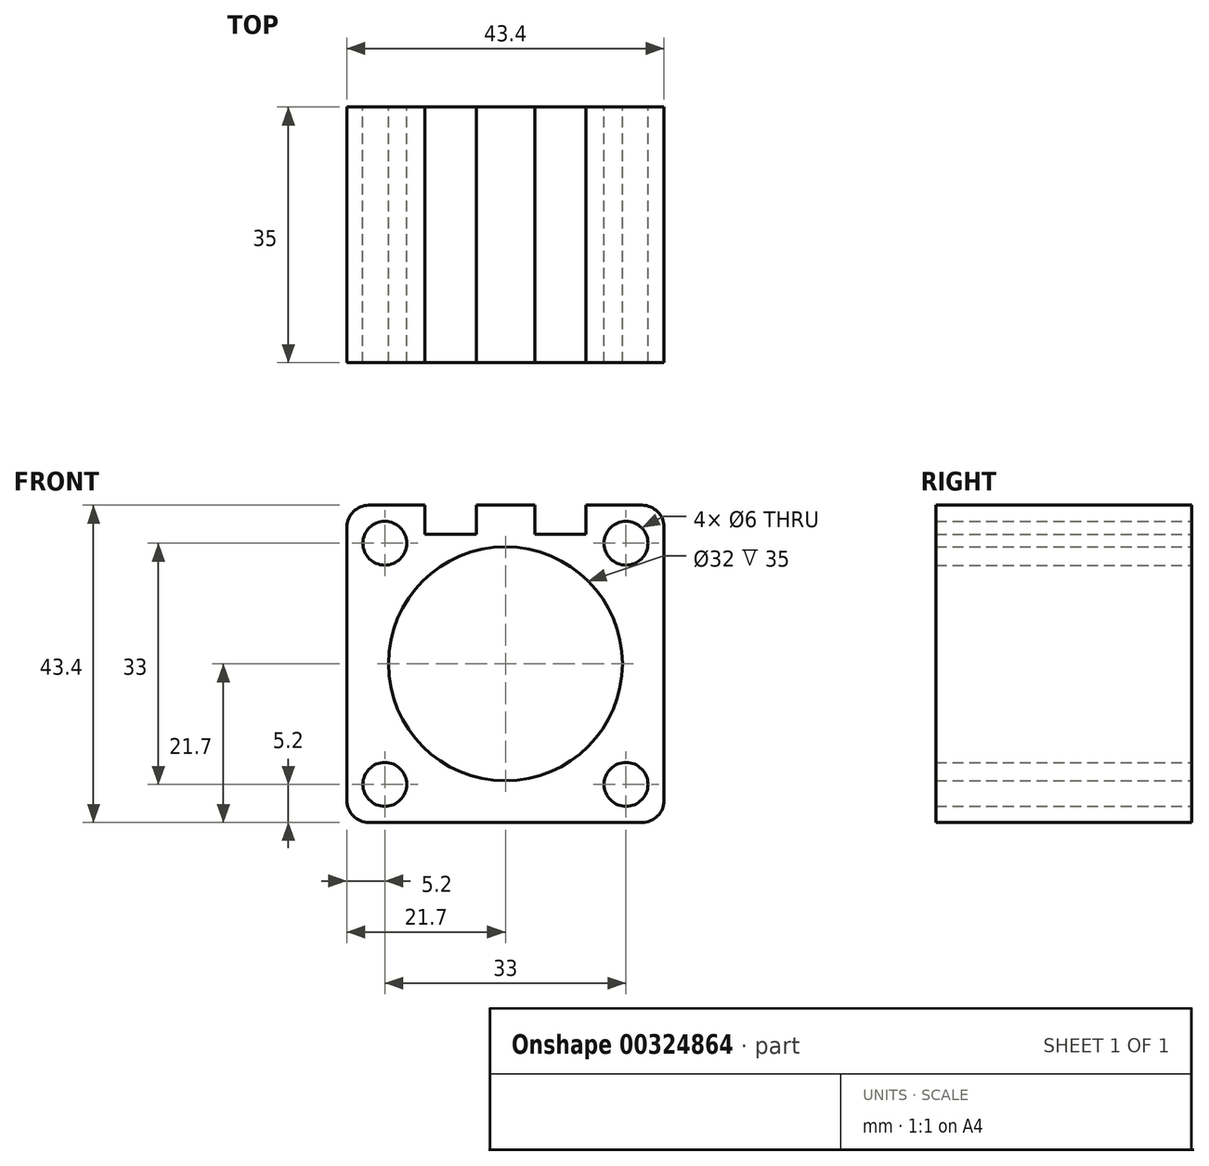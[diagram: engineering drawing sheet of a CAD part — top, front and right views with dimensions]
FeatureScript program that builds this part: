
annotation { "Feature Type Name" : "Feature", "Feature Type Description" : "" }
export const myFeature = defineFeature(function(context is Context, id is Id, definition is map)
    precondition{}
    {
        {
            var Q0;
            Q0=qCreatedBy(makeId("Front.planeOp"),FACE);
            var sketch = newSketch(context, id + "F0", { "sketchPlane" : qUnion([Q0])});
            skLineSegment(sketch, "E0.bottom", {"start": v(-21.7, 21.7) * mm, "end": v(21.7, 21.7) * mm});
            skLineSegment(sketch, "E0.top", {"start": v(-21.7, -21.7) * mm, "end": v(21.7, -21.7) * mm});
            skLineSegment(sketch, "E0.left", {"start": v(-21.7, 21.7) * mm, "end": v(-21.7, -21.7) * mm});
            skLineSegment(sketch, "E0.right", {"start": v(21.7, 21.7) * mm, "end": v(21.7, -21.7) * mm});
            skPoint(sketch, "E0.middle", {"position": v(0, 0) * mm});
            skCircle(sketch, "E1", {"center": v(0, 0) * mm, "radius": 16 * mm});
            skLineSegment(sketch, "E2", {"start": v(-21.7, 21.7) * mm, "end": v(21.7, -21.7) * mm, "construction": true});
            skLineSegment(sketch, "E3", {"start": v(-21.7, -21.7) * mm, "end": v(21.7, 21.7) * mm, "construction": true});
            skLineSegment(sketch, "E4.bottom", {"start": v(-16.5, 16.5) * mm, "end": v(16.5, 16.5) * mm, "construction": true});
            skLineSegment(sketch, "E4.top", {"start": v(-16.5, -16.5) * mm, "end": v(16.5, -16.5) * mm, "construction": true});
            skLineSegment(sketch, "E4.left", {"start": v(-16.5, 16.5) * mm, "end": v(-16.5, -16.5) * mm, "construction": true});
            skLineSegment(sketch, "E4.right", {"start": v(16.5, 16.5) * mm, "end": v(16.5, -16.5) * mm, "construction": true});
            skCircle(sketch, "E5", {"center": v(-16.5, 16.5) * mm, "radius": 3 * mm});
            skCircle(sketch, "E6", {"center": v(16.5, 16.5) * mm, "radius": 3 * mm});
            skCircle(sketch, "E7", {"center": v(-16.5, -16.5) * mm, "radius": 3 * mm});
            skCircle(sketch, "E8", {"center": v(16.5, -16.5) * mm, "radius": 3 * mm});
            skSolve(sketch);
        }
        {
            var Q0;
            Q0=makeQuery(id+"F0.imprint","IMPRINT",FACE,{"disambiguationData":[TD([[makeQuery(id+"F0.imprint","IMPRINT",EDGE,{"derivedFrom":sQuery(id+"F0.wireOp",EDGE,"E0.bottom")}),-1.0]])]});
            extrude(context, id + "F1", {"entities" : qUnion([Q0]), "depth" : 35 * mm, "symmetric" : true});
        }
        {
            var Q0;
            Q0=makeQuery(id+"F1.opExtrude","SWEPT_FACE",FACE,{"disambiguationData":[OSD([sQuery(id+"F0.wireOp",EDGE,"E0.bottom")])]});
            var sketch = newSketch(context, id + "F2", { "sketchPlane" : qUnion([Q0])});
            skLineSegment(sketch, "E9", {"start": v(0, 19.45) * mm, "end": v(0, -19.36) * mm, "construction": true});
            skPoint(sketch, "E9.endSnap0", {"position": v(0, -17.5) * mm});
            skLineSegment(sketch, "E10.bottom", {"start": v(-11, -17.5) * mm, "end": v(-4, -17.5) * mm});
            skLineSegment(sketch, "E10.top", {"start": v(-11, 17.5) * mm, "end": v(-4, 17.5) * mm});
            skLineSegment(sketch, "E10.left", {"start": v(-11, -17.5) * mm, "end": v(-11, 17.5) * mm});
            skLineSegment(sketch, "E10.right", {"start": v(-4, -17.5) * mm, "end": v(-4, 17.5) * mm});
            skLineSegment(sketch, "E11.MirrorCS", {"start": v(4, -17.5) * mm, "end": v(4, 17.5) * mm});
            skLineSegment(sketch, "E12.MirrorCS", {"start": v(11, -17.5) * mm, "end": v(11, 17.5) * mm});
            skLineSegment(sketch, "E13.MirrorCS", {"start": v(11, 17.5) * mm, "end": v(4, 17.5) * mm});
            skLineSegment(sketch, "E14.MirrorCS", {"start": v(11, -17.5) * mm, "end": v(4, -17.5) * mm});
            skSolve(sketch);
        }
        {
            var Q0;
            Q0=makeQuery(id+"F2.imprint","IMPRINT",FACE,{"disambiguationData":[TD([[makeQuery(id+"F2.imprint","IMPRINT",EDGE,{"derivedFrom":sQuery(id+"F2.wireOp",EDGE,"E10.bottom")}),1.0]])]});
            var Q1;
            Q1=makeQuery(id+"F2.imprint","IMPRINT",FACE,{"disambiguationData":[TD([[makeQuery(id+"F2.imprint","IMPRINT",EDGE,{"derivedFrom":sQuery(id+"F2.wireOp",EDGE,"E11.MirrorCS")}),-1.0]])]});
            extrude(context, id + "F3", {"entities" : qUnion([Q0, Q1]), "operationType" : NewBodyOperationType.REMOVE, "oppositeDirection" : true, "depth" : 4 * mm});
        }
        {
            var Q0;
            Q0=makeQuery(id+"F1.opExtrude","SWEPT_EDGE",EDGE,{"disambiguationData":[OSD([sQuery(id+"F0.wireOp",EDGE,"E0.bottom"),sQuery(id+"F0.wireOp",EDGE,"E0.left")])]});
            var Q1;
            Q1=makeQuery(id+"F1.opExtrude","SWEPT_EDGE",EDGE,{"disambiguationData":[OSD([sQuery(id+"F0.wireOp",EDGE,"E0.bottom"),sQuery(id+"F0.wireOp",EDGE,"E0.right")])]});
            var Q2;
            Q2=makeQuery(id+"F1.opExtrude","SWEPT_EDGE",EDGE,{"disambiguationData":[OSD([sQuery(id+"F0.wireOp",EDGE,"E0.top"),sQuery(id+"F0.wireOp",EDGE,"E0.right")])]});
            var Q3;
            Q3=makeQuery(id+"F1.opExtrude","SWEPT_EDGE",EDGE,{"disambiguationData":[OSD([sQuery(id+"F0.wireOp",EDGE,"E0.top"),sQuery(id+"F0.wireOp",EDGE,"E0.left")])]});
            fillet(context, id + "F4", {"entities" : qUnion([Q0, Q1, Q2, Q3]), "radius" : 3 * mm, "tangentPropagation" : true, "allowEdgeOverflow" : false});
        }
    });
